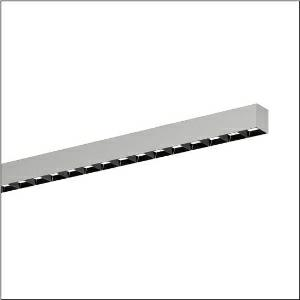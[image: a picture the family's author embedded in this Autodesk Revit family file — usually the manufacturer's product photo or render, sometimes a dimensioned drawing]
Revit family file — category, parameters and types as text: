
# Revit family: silica_21_51mx22dc4asb
name_source: partatom
category: Lighting Fixtures
units: mm (PartAtom-declared; Revit-internal decimal feet)

## family parameters
Cut with Voids When Loaded = No
Host = Face
Light Source = No
Part Type = Normal
Room Calculation Point = No
Round Connector Dimension = Use Diameter
Shared = No

## types (1)
- --- (1 x LED, 10800 lm, 64.7 W, 4000K)
    Apparent Load = 65 VA
    CIE Flux Codes = 86 100 100 100 100
    Color Rendering = 80
    Color Temperature = 4000K
    Default Elevation = 1800 mm
    Description = Silica 21, office luminaire, primary light control with darklight reflector, of PMMA, black, CAT 2 (L<= 3000cd/m²), light emission: direct distribution, primary light characteristic: symmetric, installation type: surface-mounted, LED, rated luminous flux: 10.800lm, luminous efficacy: 167lm/W, light colour: 840, colour temperature: 4000K, control gear: DALI 2, with terminal, 3+2-pole, max. 2.5mm², mains connection: 220..240V, AC, 50/60Hz, rated input power: 64.7W, luminaire housing, of aluminium, metallic grey (RAL 9006), length: 3.004mm, width: 53mm, height: 53mm, protection rating (complete): IP20, insulation class (complete): insulation class I (protective earthing), certification: CE, permissible operating ambient temperature: 0..+35°C, standard: EN 50419, packaging unit: 1 piece
    Height = 53 mm
    Lamp = 1 x LED
    Lamp Light Flux = 10800 lm
    Lamp Power = 64.7 W
    Lamp count = 1
    Length = 3004 mm
    Luminous efficacy = 167 lm/W
    Manufacturer = Siteco
    ModVariant = No
    Model = 51MX22DC4ASB
    Mounting Place = Ceiling
    Mounting Type = Surface mounted
    Number of Poles = 1
    OnlyDefault = Yes
    Power Factor = 1
    Product Name = Silica 21
    Product group = office luminaire | ceiling mounted
    ProductGroupID = 301
    Protection Class = Protection class I
    Protection Degree = IP 20
    RLX_Detail_Level = 1
    RLX_Emergency_Light_Flux = 0 lm
    RLX_Emergency_Type = 0
    RLX_Emergency_Type_DB = No
    RlxData = <blob elided: 63129 chars, md5=f1ce92c1>
    Socket = socket
    Standby Power = 0 W
    System Light Flux = 10800 lm
    System Power = 65 W
    Type Comments = factory setting: luminous flux: 100 % | dim-lin: 254 | 366 mA
    Type Image = l_1335929.jpg
    URL = http://relux.com
    VarID = @adj_124713
    Voltage = 0 V
    Weight = 0.00 kg
    Width = 53 mm

## geometry (parser evidence)
native form markers: Blend x4, Sweep x11
no freeform markers — native parametric forms only
